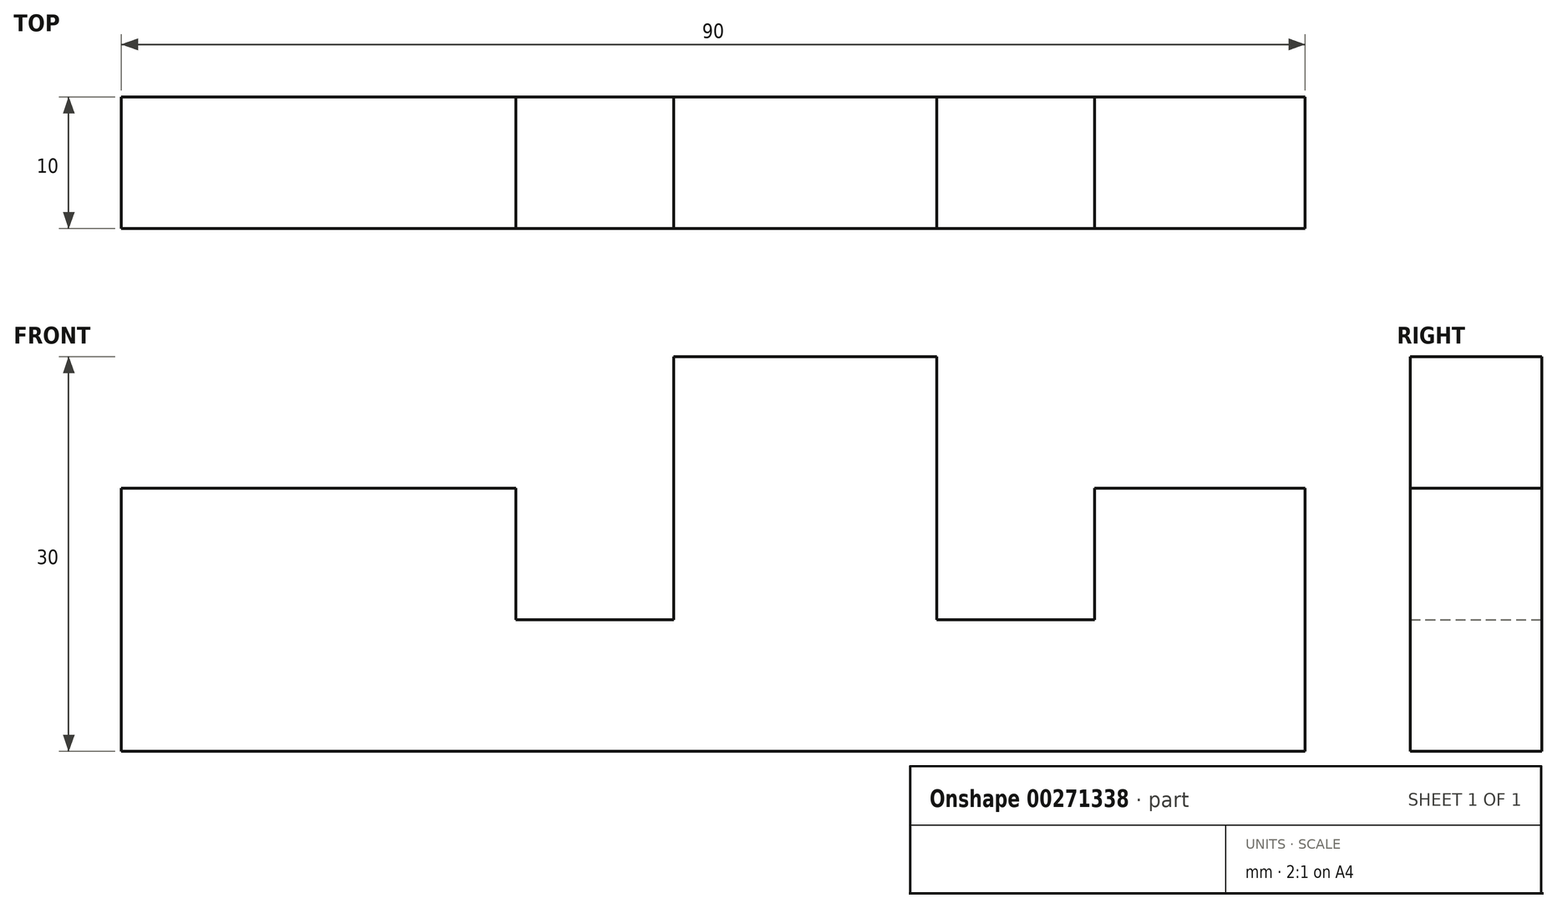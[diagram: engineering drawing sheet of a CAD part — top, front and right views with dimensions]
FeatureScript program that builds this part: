
annotation { "Feature Type Name" : "Feature", "Feature Type Description" : "" }
export const myFeature = defineFeature(function(context is Context, id is Id, definition is map)
    precondition{}
    {
        {
            var Q0;
            Q0=qCreatedBy(makeId("Front.planeOp"),FACE);
            var sketch = newSketch(context, id + "F0", { "sketchPlane" : qUnion([Q0])});
            skLineSegment(sketch, "E0", {"start": v(0, 0) * mm, "end": v(90, 0) * mm});
            skLineSegment(sketch, "E1", {"start": v(0, 0) * mm, "end": v(0, 20) * mm});
            skLineSegment(sketch, "E2", {"start": v(90, 0) * mm, "end": v(90, 20) * mm});
            skLineSegment(sketch, "E3", {"start": v(90, 20) * mm, "end": v(74, 20) * mm});
            skLineSegment(sketch, "E4", {"start": v(74, 20) * mm, "end": v(74, 10) * mm});
            skLineSegment(sketch, "E5", {"start": v(74, 10) * mm, "end": v(62, 10) * mm});
            skLineSegment(sketch, "E6", {"start": v(62, 10) * mm, "end": v(62, 30) * mm});
            skLineSegment(sketch, "E7", {"start": v(62, 30) * mm, "end": v(42, 30) * mm});
            skLineSegment(sketch, "E8", {"start": v(42, 30) * mm, "end": v(42, 10) * mm});
            skLineSegment(sketch, "E9", {"start": v(42, 10) * mm, "end": v(30, 10) * mm});
            skLineSegment(sketch, "E10", {"start": v(30, 10) * mm, "end": v(30, 20) * mm});
            skLineSegment(sketch, "E11", {"start": v(30, 20) * mm, "end": v(0, 20) * mm});
            skSolve(sketch);
        }
        {
            var Q0;
            Q0 = qSketchRegion(id + "F0", true);
            extrude(context, id + "F1", {"entities" : qUnion([Q0]), "depth" : 10 * mm});
        }
    });
